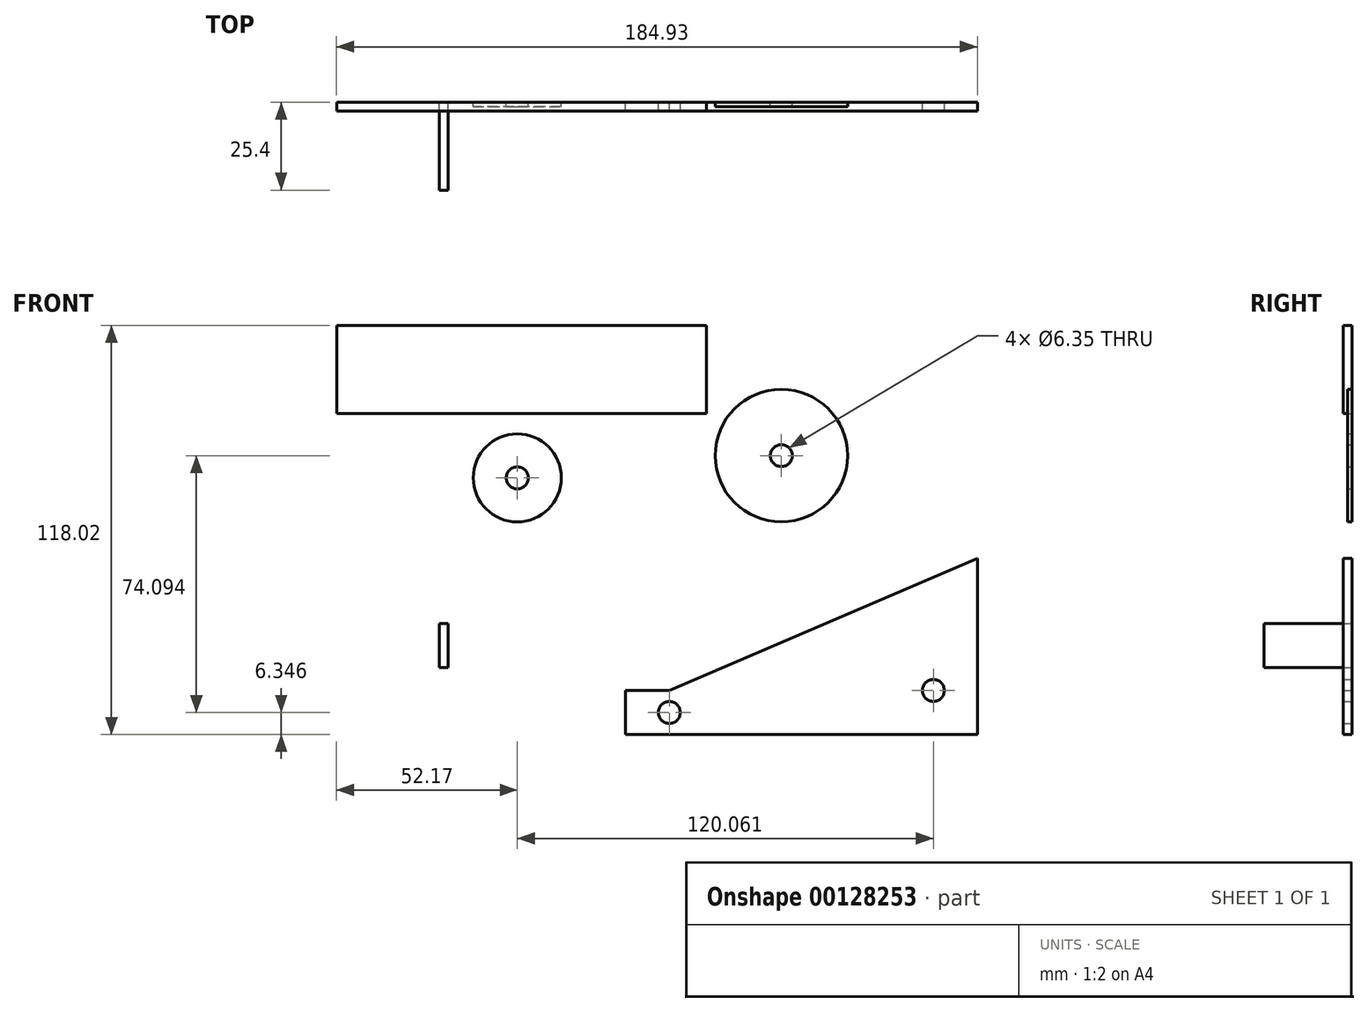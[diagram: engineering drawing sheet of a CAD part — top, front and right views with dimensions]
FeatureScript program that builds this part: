
annotation { "Feature Type Name" : "Feature", "Feature Type Description" : "" }
export const myFeature = defineFeature(function(context is Context, id is Id, definition is map)
    precondition{}
    {
        {
            var Q0;
            Q0=qCreatedBy(makeId("Front.planeOp"),FACE);
            var sketch = newSketch(context, id + "F0", { "sketchPlane" : qUnion([Q0])});
            skCircle(sketch, "E0", {"center": v(-38.1, 6.29) * mm, "radius": 3.18 * mm});
            skCircle(sketch, "E1", {"center": v(38.1, 12.7) * mm, "radius": 3.18 * mm});
            skCircle(sketch, "E2", {"center": v(-38.1, 6.29) * mm, "radius": 12.7 * mm});
            skCircle(sketch, "E3", {"center": v(38.1, 12.7) * mm, "radius": 19.11 * mm});
            skLineSegment(sketch, "E4", {"start": v(43.86, -67.74) * mm, "end": v(-6.94, -67.74) * mm});
            skLineSegment(sketch, "E5", {"start": v(43.86, -67.74) * mm, "end": v(94.66, -67.74) * mm});
            skLineSegment(sketch, "E6", {"start": v(94.66, -67.74) * mm, "end": v(94.66, -16.94) * mm});
            skLineSegment(sketch, "E7", {"start": v(-6.94, -67.74) * mm, "end": v(-6.94, -55.04) * mm});
            skCircle(sketch, "E8", {"center": v(5.76, -61.4) * mm, "radius": 3.18 * mm});
            skCircle(sketch, "E9", {"center": v(81.96, -55.04) * mm, "radius": 3.18 * mm});
            skLineSegment(sketch, "E10", {"start": v(-58.11, -35.71) * mm, "end": v(-58.11, -48.41) * mm});
            skLineSegment(sketch, "E11", {"start": v(-58.11, -48.41) * mm, "end": v(-60.65, -48.41) * mm});
            skLineSegment(sketch, "E12", {"start": v(-60.65, -48.41) * mm, "end": v(-60.65, -35.71) * mm});
            skLineSegment(sketch, "E13", {"start": v(-60.65, -35.71) * mm, "end": v(-58.11, -35.71) * mm});
            skLineSegment(sketch, "E14", {"start": v(-6.94, -55.04) * mm, "end": v(5.76, -55.04) * mm});
            skLineSegment(sketch, "E15", {"start": v(5.76, -55.04) * mm, "end": v(94.66, -16.94) * mm});
            skLineSegment(sketch, "E16", {"start": v(-90.27, 24.88) * mm, "end": v(16.41, 24.88) * mm});
            skLineSegment(sketch, "E17", {"start": v(16.41, 24.88) * mm, "end": v(16.41, 50.28) * mm});
            skLineSegment(sketch, "E18", {"start": v(16.41, 50.28) * mm, "end": v(-90.27, 50.28) * mm});
            skLineSegment(sketch, "E19", {"start": v(-90.27, 50.28) * mm, "end": v(-90.27, 24.88) * mm});
            skSolve(sketch);
        }
        {
            var Q0;
            Q0=makeQuery(id+"F0.imprint","IMPRINT",FACE,{"disambiguationData":[TD([[makeQuery(id+"F0.imprint","IMPRINT",EDGE,{"derivedFrom":sQuery(id+"F0.wireOp",EDGE,"E0")}),-1.0]])]});
            var Q1;
            Q1=makeQuery(id+"F0.imprint","IMPRINT",FACE,{"disambiguationData":[TD([[makeQuery(id+"F0.imprint","IMPRINT",EDGE,{"derivedFrom":sQuery(id+"F0.wireOp",EDGE,"E1")}),-1.0]])]});
            extrude(context, id + "F1", {"entities" : qUnion([Q0, Q1]), "depth" : 1.27 * mm});
        }
        {
            var Q0;
            Q0=makeQuery(id+"F0.imprint","IMPRINT",FACE,{"disambiguationData":[TD([[makeQuery(id+"F0.imprint","IMPRINT",EDGE,{"derivedFrom":sQuery(id+"F0.wireOp",EDGE,"E4")}),-1.0]])]});
            extrude(context, id + "F2", {"entities" : qUnion([Q0]), "depth" : 2.54 * mm});
        }
        {
            var Q0;
            Q0=makeQuery(id+"F0.imprint","IMPRINT",FACE,{"disambiguationData":[TD([[makeQuery(id+"F0.imprint","IMPRINT",EDGE,{"derivedFrom":sQuery(id+"F0.wireOp",EDGE,"E10")}),-1.0]])]});
            extrude(context, id + "F3", {"entities" : qUnion([Q0]), "depth" : 25.4 * mm});
        }
        {
            var Q0;
            Q0=makeQuery(id+"F0.imprint","IMPRINT",FACE,{"disambiguationData":[TD([[makeQuery(id+"F0.imprint","IMPRINT",EDGE,{"derivedFrom":sQuery(id+"F0.wireOp",EDGE,"E16")}),1.0]])]});
            extrude(context, id + "F4", {"entities" : qUnion([Q0]), "depth" : 2.54 * mm});
        }
    });
